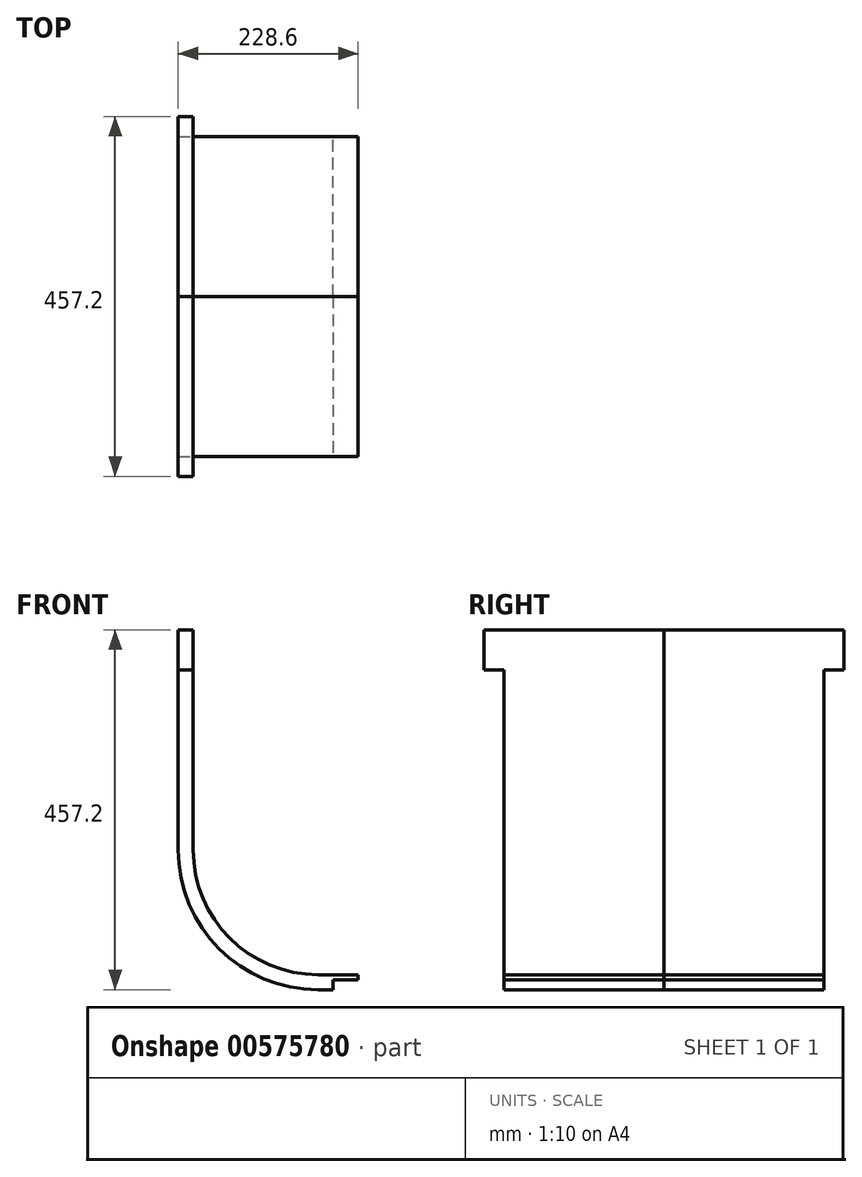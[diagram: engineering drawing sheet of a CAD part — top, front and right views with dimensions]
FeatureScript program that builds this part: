
annotation { "Feature Type Name" : "Feature", "Feature Type Description" : "" }
export const myFeature = defineFeature(function(context is Context, id is Id, definition is map)
    precondition{}
    {
        {
            var Q0;
            Q0=qCreatedBy(makeId("Front.planeOp"),FACE);
            var sketch = newSketch(context, id + "F0", { "sketchPlane" : qUnion([Q0])});
            skLineSegment(sketch, "E0", {"start": v(-586.54, 457.2) * mm, "end": v(-357.94, 457.2) * mm});
            skLineSegment(sketch, "E1", {"start": v(-357.94, 457.2) * mm, "end": v(-357.94, 0) * mm});
            skLineSegment(sketch, "E2", {"start": v(-357.94, 0) * mm, "end": v(-586.54, 0) * mm});
            skLineSegment(sketch, "E3", {"start": v(-586.54, 0) * mm, "end": v(-586.54, 457.2) * mm});
            skLineSegment(sketch, "E4", {"start": v(-567.5, 457.2) * mm, "end": v(-567.5, 177.8) * mm});
            skLineSegment(sketch, "E5", {"start": v(-357.94, 19.05) * mm, "end": v(-408.74, 19.05) * mm});
            skArc(sketch, "E6", {"start": v(-567.5, 177.8) * mm, "mid": v(-521, 65.55) * mm, "end": v(-408.74, 19.05) * mm});
            skArc(sketch, "E7", {"start": v(-586.54, 177.8) * mm, "mid": v(-534.47, 52.08) * mm, "end": v(-408.74, 0) * mm});
            skLineSegment(sketch, "E8", {"start": v(-586.54, 406.4) * mm, "end": v(-567.5, 406.4) * mm});
            skSolve(sketch);
        }
        {
            var Q0;
            {var subQ8=sQuery(id+"F0.wireOp",EDGE,"E5");Q0=makeQuery(id+"F0.imprint","IMPRINT",FACE,{"disambiguationData":[TD([[makeQuery(id+"F0.imprint","IMPRINT",EDGE,{"derivedFrom":subQ8}),1.0]])]});}
            extrude(context, id + "F1", {"entities" : qUnion([Q0]), "depth" : 203.2 * mm, "offsetDistance" : 25.4 * mm});
        }
        {
            var Q0;
            {var subQ5=sQuery(id+"F0.wireOp",EDGE,"E8");Q0=makeQuery(id+"F0.imprint","IMPRINT",FACE,{"disambiguationData":[TD([[makeQuery(id+"F0.imprint","IMPRINT",EDGE,{"derivedFrom":subQ5}),1.0]])]});}
            extrude(context, id + "F2", {"entities" : qUnion([Q0]), "operationType" : NewBodyOperationType.ADD, "depth" : 228.6 * mm, "offsetDistance" : 25.4 * mm});
        }
        {
            var Q0;
            Q0=makeQuery(id+"F1.opExtrude","SWEPT_BODY",BODY,{"disambiguationData":[OSD([sQuery(id+"F0.wireOp",EDGE,"E1"),sQuery(id+"F0.wireOp",EDGE,"E2"),sQuery(id+"F0.wireOp",EDGE,"E3"),sQuery(id+"F0.wireOp",EDGE,"E4"),sQuery(id+"F0.wireOp",EDGE,"E5"),sQuery(id+"F0.wireOp",EDGE,"E6"),sQuery(id+"F0.wireOp",EDGE,"E7"),sQuery(id+"F0.wireOp",EDGE,"E8")])]});
            var Q1;
            {var subQ7=sQuery(id+"F0.wireOp",EDGE,"E5");Q1=makeQuery(id+"F0.imprint","IMPRINT",FACE,{"disambiguationData":[TD([[makeQuery(id+"F0.imprint","IMPRINT",EDGE,{"derivedFrom":subQ7}),-1.0]])]});}
            mirror(context, id + "F3", {"entities" : qUnion([Q0]), "mirrorPlane" : qUnion([Q1])});
        }
        {
            var Q0;
            Q0=makeQuery(id+"F3.opPattern","COPY",FACE,{"derivedFrom":makeQuery(id+"F1.opExtrude","SWEPT_FACE",FACE,{"disambiguationData":[OSD([sQuery(id+"F0.wireOp",EDGE,"E2")])]}),"instanceName":"1"});
            var sketch = newSketch(context, id + "F4", { "sketchPlane" : qUnion([Q0])});
            skLineSegment(sketch, "E9", {"start": v(-357.94, 0) * mm, "end": v(-389.69, 0) * mm});
            skLineSegment(sketch, "E10", {"start": v(-389.69, 0) * mm, "end": v(-389.69, -203.2) * mm});
            skLineSegment(sketch, "E11", {"start": v(-389.69, -203.2) * mm, "end": v(-357.94, -203.2) * mm});
            skLineSegment(sketch, "E12", {"start": v(-357.94, -203.2) * mm, "end": v(-357.94, 0) * mm});
            skSolve(sketch);
        }
        {
            var Q0;
            Q0=makeQuery(id+"F4.imprint","IMPRINT",FACE,{"disambiguationData":[TD([[makeQuery(id+"F4.imprint","IMPRINT",EDGE,{"derivedFrom":sQuery(id+"F4.wireOp",EDGE,"E9")}),1.0]])]});
            extrude(context, id + "F5", {"entities" : qUnion([Q0]), "operationType" : NewBodyOperationType.REMOVE, "oppositeDirection" : true, "depth" : 12.7 * mm, "offsetDistance" : 25.4 * mm});
        }
        {
            var Q0;
            Q0=makeQuery(id+"F1.opExtrude","SWEPT_FACE",FACE,{"disambiguationData":[OSD([sQuery(id+"F0.wireOp",EDGE,"E2")])]});
            var sketch = newSketch(context, id + "F6", { "sketchPlane" : qUnion([Q0])});
            skLineSegment(sketch, "E13", {"start": v(-389.7, 0) * mm, "end": v(-389.7, 203.2) * mm});
            skLineSegment(sketch, "E14", {"start": v(-389.7, 203.2) * mm, "end": v(-357.94, 203.2) * mm});
            skLineSegment(sketch, "E15", {"start": v(-357.94, 203.2) * mm, "end": v(-357.94, 0) * mm});
            skLineSegment(sketch, "E16", {"start": v(-357.94, 0) * mm, "end": v(-389.7, 0) * mm});
            skSolve(sketch);
        }
        {
            var Q0;
            Q0=makeQuery(id+"F4.imprint","IMPRINT",FACE,{"disambiguationData":[TD([[makeQuery(id+"F4.imprint","IMPRINT",EDGE,{"derivedFrom":sQuery(id+"F4.wireOp",EDGE,"E9")}),1.0]])]});
            var Q1;
            Q1=makeQuery(id+"F6.imprint","IMPRINT",FACE,{"disambiguationData":[TD([[makeQuery(id+"F6.imprint","IMPRINT",EDGE,{"derivedFrom":sQuery(id+"F6.wireOp",EDGE,"E13")}),-1.0]])]});
            extrude(context, id + "F7", {"entities" : qUnion([Q0, Q1]), "operationType" : NewBodyOperationType.REMOVE, "oppositeDirection" : true, "depth" : 12.7 * mm, "offsetDistance" : 25.4 * mm});
        }
    });
